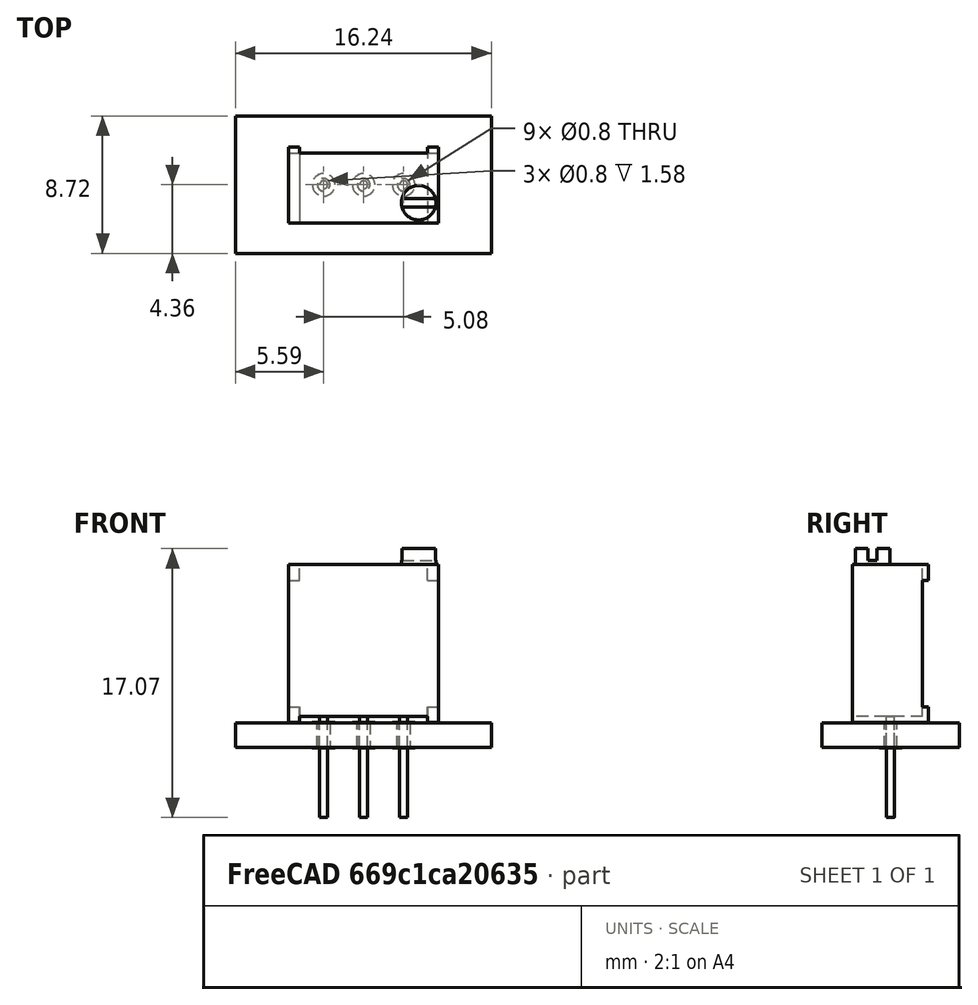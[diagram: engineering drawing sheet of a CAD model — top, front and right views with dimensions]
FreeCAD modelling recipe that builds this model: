
FCSTD DOCUMENT  (FreeCAD 0.18R15611 (Git))
Label: Potentiometer_Bourns_3296W_Vertical
License: All rights reserved
LicenseURL: http://en.wikipedia.org/wiki/All_rights_reserved
objects: Part::FeaturePython×7, Part::Box×6, Part::Cylinder×4, Part::MultiFuse×2, App::DocumentObjectGroup×1, Part::Cut×1, Part::Feature×1
note: 21 computed .brp shape members not serialized (recipe doc carries the construction recipe); baked Part::Feature solids carry a one-line shape summary decoded from their .brp

FEATURE [Part::FeaturePython] FCrtYd_lines  label="FCrtYd"  # a2plus imported part (geometry in sourceFile) (typed FeaturePython)
  fixedPosition = true
FEATURE [Part::FeaturePython] FFab_lines  label="FFab"  # a2plus imported part (geometry in sourceFile) (typed FeaturePython)
  fixedPosition = true
FEATURE [Part::FeaturePython] Filk_lines  label="FrontSilk"  # a2plus imported part (geometry in sourceFile) (typed FeaturePython)
  fixedPosition = true
FEATURE [Part::FeaturePython] TopPads  # a2plus imported part (geometry in sourceFile) (typed FeaturePython)
  fixedPosition = true
FEATURE [Part::FeaturePython] BotPads  # a2plus imported part (geometry in sourceFile) (typed FeaturePython)
  fixedPosition = true
FEATURE [Part::FeaturePython] THPs  label="PTHs"  # a2plus imported part (geometry in sourceFile) (typed FeaturePython)
  fixedPosition = true
FEATURE [Part::FeaturePython] newPCB  label="Pcb"  # a2plus imported part (geometry in sourceFile) (typed FeaturePython)
  fixedPosition = true
FEATURE [App::DocumentObjectGroup] Potentiometer_Bourns_3296W_Vertical_fp
  Group = -> [FCrtYd_lines,FFab_lines,Filk_lines,TopPads,BotPads,THPs,newPCB]
FEATURE [Part::Box] Box006  label="StandoffFront001"
  AttacherType = Attacher::AttachEngine3D
  Height = 4.83
  Length = 1
  Placement = pos=(0,8.83,0) rot=(0,0,1;0rad)
  Width = 0.7
FEATURE [Part::Box] Box  label="Body"
  AttacherType = Attacher::AttachEngine3D
  Height = 4.45
  Length = 9.65
  Placement = pos=(0,0,0.38) rot=(0,0,1;0rad)
  Width = 9.53
FEATURE [Part::Box] Box007  label="StandoffBack001"
  AttacherType = Attacher::AttachEngine3D
  Height = 4.83
  Length = 1
  Placement = pos=(9.03,8.83,0) rot=(0,0,1;0rad)
  Width = 0.7
FEATURE [Part::Box] Box003  label="Cube001"
  AttacherType = Attacher::AttachEngine3D
  Height = 0.76
  Length = 10
  Placement = pos=(-5,-2.54,7.5) rot=(0,0,1;0rad)
  Width = 0.56
FEATURE [Part::Box] Box005  label="StandoffBack"
  AttacherType = Attacher::AttachEngine3D
  Height = 4.83
  Length = 1
  Placement = pos=(9.03,0,0) rot=(0,0,1;0rad)
  Width = 0.7
FEATURE [Part::Box] Box004  label="StandoffFront"
  AttacherType = Attacher::AttachEngine3D
  Height = 4.83
  Length = 1
  Width = 0.7
FEATURE [Part::MultiFuse] Fusion  label="FusionBody"
  Placement = pos=(-7.305,2.41,10.03) rot=(0.57735,0.57735,-0.57735;2.0944rad)
  Refine = true
  Shapes = -> [Box,Box004,Box005,Box006,Box007]
FEATURE [Part::Cylinder] Cylinder  label="Pin1"
  Angle = 360
  AttacherType = Attacher::AttachEngine3D
  Height = 6.4
  Placement = pos=(0,0,-6.02) rot=(0,0,1;0rad)
  Radius = 0.255
FEATURE [Part::Cylinder] Cylinder003  label="Knob"
  Angle = 360
  AttacherType = Attacher::AttachEngine3D
  Height = 1.02
  Placement = pos=(-0.405,-2.25,7.24) rot=(0,0,1;0rad)
  Radius = 1.095
FEATURE [Part::Cut] Cut  label="CutKnob"
  Base = -> Cylinder003
  Placement = pos=(1.36,1.11,2.79) rot=(0,-1,0;0rad)
  Refine = true
  Tool = -> Box003
FEATURE [Part::Cylinder] Cylinder002  label="Pin2"
  Angle = 360
  AttacherType = Attacher::AttachEngine3D
  Height = 6.4
  Placement = pos=(-2.54,0,-6.02) rot=(0,0,1;0rad)
  Radius = 0.255
FEATURE [Part::Cylinder] Cylinder001  label="Pin3"
  Angle = 360
  AttacherType = Attacher::AttachEngine3D
  Height = 6.4
  Placement = pos=(-5.08,0,-6.02) rot=(0,0,1;0rad)
  Radius = 0.255
FEATURE [Part::MultiFuse] FusionBody_mp_cp  label="FusionBody_fd"
  Refine = true
  Shapes = -> [Fusion,Cylinder,Cylinder001,Cut,Cylinder002]
FEATURE [Part::Feature] Shape  label="Potentiometer_Bourns_3296W_Vertical"
  shape: bbox 9.53 x 4.83 x 17.07 mm, 32 faces (baked)
